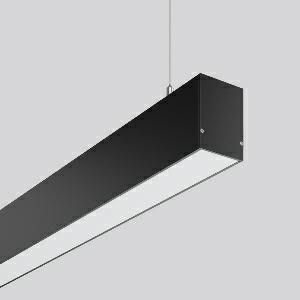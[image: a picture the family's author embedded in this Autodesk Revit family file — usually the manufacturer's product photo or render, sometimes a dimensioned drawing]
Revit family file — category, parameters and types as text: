
# Revit family: less_is_more_50_312314_003_1_76_1b10
name_source: partatom
category: Lighting Fixtures
units: mm (PartAtom-declared; Revit-internal decimal feet)

## family parameters
Cut with Voids When Loaded = No
Host = Face
Light Source = No
Part Type = Normal
Room Calculation Point = No
Round Connector Dimension = Use Diameter
Shared = No

## types (1)
- LESS IS MORE 50 (1 x LED Modul 840, 4850 lm, 4000)
    Apparent Load = 40 VA
    CIE Flux Codes = 48 79 95 100 100
    Color Rendering = 80
    Color Temperature = 4000
    Default Elevation = 1800 mm
    Description = Series: LESS IS MORE 50
Linear pendant luminaire for aesthetically sophisticated lighting. Housing: extruded aluminium profile, powder-coated. End cap aluminium powder-coated. Canopy made of aluminium, powder-coated. Diffuser made of non-yellowing plastic (PMMA), opal. Direct light emission. Suitable for pendant. 2-point steel cable suspension freely positionable and infinitely height-adjustable. Special lengths available on request. LED unit with integrated converter interchangeable and removable. Suitable for through-wiring. With sensors or as a safety luminaire on request. 
Colour: deep black, matt (RAL 9005)
Length: 1687 mm
Width: 57 mm
Height: 75 mm
Suspension length: 2000 mm
Lamp: LED
Socket: without socket
Colour temperature: 4000K
Colour rendering index (CRI): 80
System power: 40 W
Rated luminous flux: 4850 lm
Luminous efficiency: 121 lm/W
Control gear: Converter, dimmable, DALI
Protection class: I
Type of protection: IP 20
    Height = 75 mm
    Lamp = 1 x LED Modul 840
    Lamp Light Flux = 4850 lm
    Lamp count = 1
    Length = 1687 mm
    Lifetime = 50000 h
    Luminous efficacy = 121 lm/W
    Manufacturer = RZB
    ModVariant = No
    Model = 312314.003.1.76
    Mounting Place = Ceiling
    Mounting Type = Pendant
    Number of Poles = 1
    OnlyDefault = Yes
    Power Factor = 1
    Product Name = LESS IS MORE 50
    Product group = Pendant LED linear luminaires
    ProductGroupID = 907
    Protection Class = Protection class I
    Protection Degree = IP 20
    RLX_Detail_Level = 1
    RLX_Emergency_Light_Flux = 0 lm
    RLX_Emergency_Type = 0
    RLX_Emergency_Type_DB = No
    RlxData = <blob elided: 28861 chars, md5=1a74960d>
    Socket = socket
    Standby Power = 0 W
    System Light Flux = 4850 lm
    System Power = 40 W
    Type Comments = Product without accessories
    Type Image = 312318.003.jpg
    URL = http://relux.com
    VarID = ---
    Voltage = 230 V
    Voltage Range = 220-240 V
    Weight = 0.00 kg
    Width = 57 mm

## geometry (parser evidence)
native form markers: Blend x4, Sweep x11
no freeform markers — native parametric forms only
